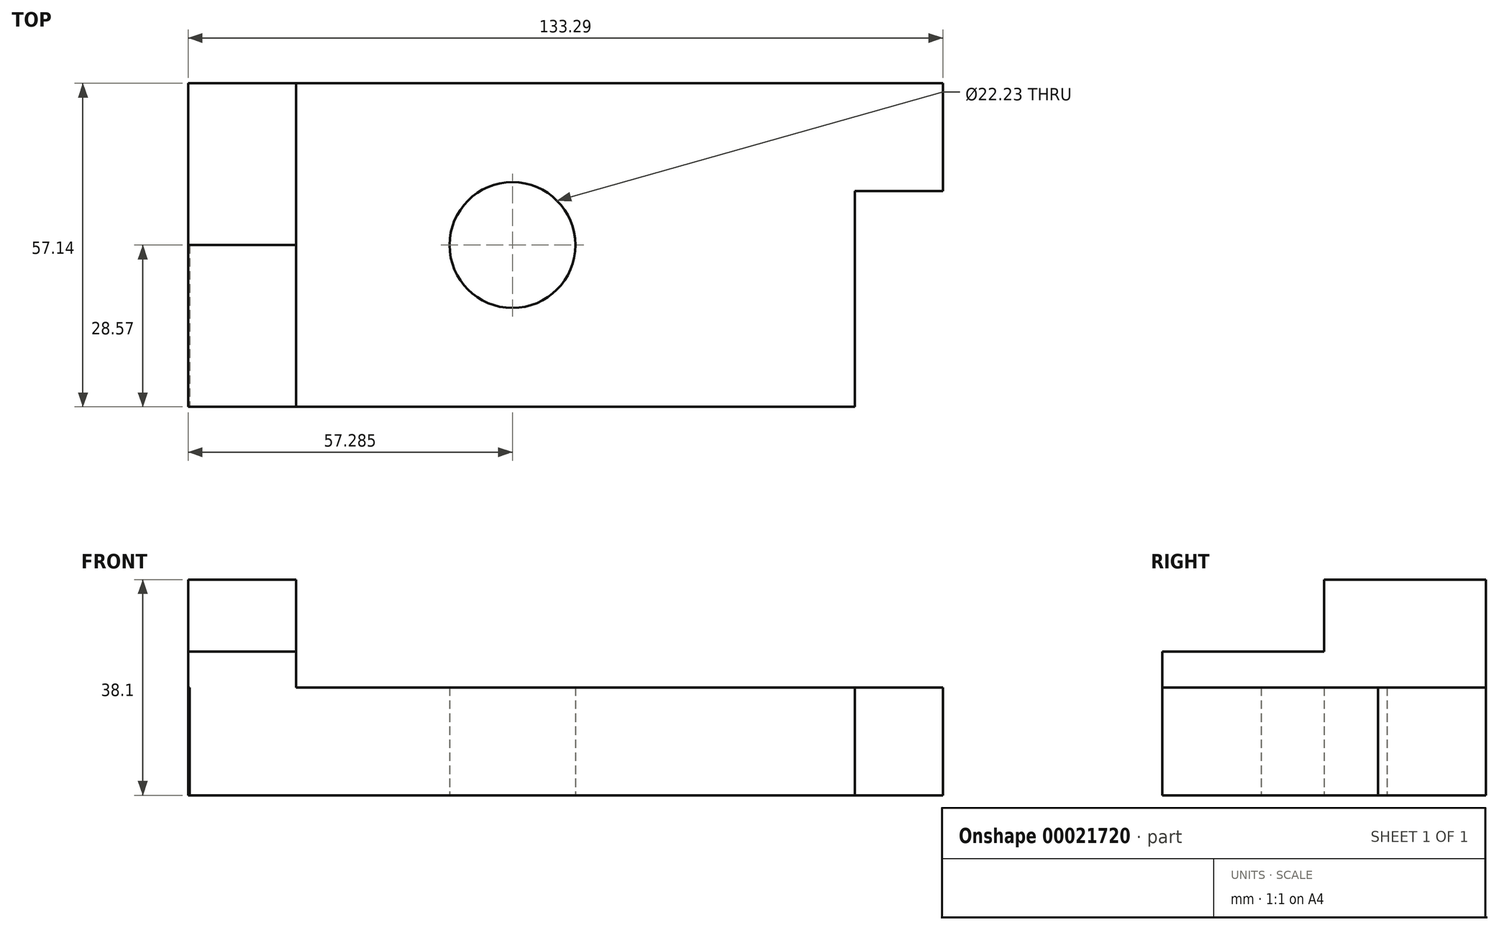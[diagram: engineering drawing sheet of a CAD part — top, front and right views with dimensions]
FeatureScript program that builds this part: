
annotation { "Feature Type Name" : "Feature", "Feature Type Description" : "" }
export const myFeature = defineFeature(function(context is Context, id is Id, definition is map)
    precondition{}
    {
        {
            var Q0;
            Q0=qCreatedBy(makeId("Top.planeOp"),FACE);
            var sketch = newSketch(context, id + "F0", { "sketchPlane" : qUnion([Q0])});
            skLineSegment(sketch, "E0.bottom", {"start": v(0, 0) * mm, "end": v(-0.06, 0) * mm});
            skLineSegment(sketch, "E0.top", {"start": v(0, 28.58) * mm, "end": v(-0.06, 28.58) * mm});
            skLineSegment(sketch, "E0.left", {"start": v(0, 0) * mm, "end": v(0, 28.58) * mm});
            skLineSegment(sketch, "E0.right", {"start": v(-0.06, 0) * mm, "end": v(-0.06, 28.58) * mm});
            skLineSegment(sketch, "E1.bottom", {"start": v(0, 0) * mm, "end": v(114.24, 0) * mm});
            skLineSegment(sketch, "E1.top", {"start": v(0, 28.57) * mm, "end": v(114.24, 28.58) * mm});
            skLineSegment(sketch, "E1.left", {"start": v(0, 0) * mm, "end": v(0, 28.57) * mm});
            skLineSegment(sketch, "E1.right", {"start": v(114.24, 0) * mm, "end": v(114.24, 28.58) * mm});
            skLineSegment(sketch, "E2.bottom", {"start": v(0.27, 0) * mm, "end": v(0, 0) * mm});
            skLineSegment(sketch, "E2.top", {"start": v(0.27, -28.57) * mm, "end": v(0, -28.57) * mm});
            skLineSegment(sketch, "E2.left", {"start": v(0, 0) * mm, "end": v(0, -28.57) * mm});
            skLineSegment(sketch, "E2.right", {"start": v(0.27, 0) * mm, "end": v(0.27, -28.57) * mm});
            skLineSegment(sketch, "E3.bottom", {"start": v(0, 0) * mm, "end": v(114.57, 0) * mm});
            skLineSegment(sketch, "E3.top", {"start": v(0, -28.58) * mm, "end": v(114.57, -28.57) * mm});
            skLineSegment(sketch, "E3.left", {"start": v(0, 0) * mm, "end": v(0, -28.58) * mm});
            skLineSegment(sketch, "E3.right", {"start": v(114.57, 0) * mm, "end": v(114.57, -28.57) * mm});
            skLineSegment(sketch, "E4.bottom", {"start": v(114.57, -28.57) * mm, "end": v(98.7, -28.57) * mm});
            skLineSegment(sketch, "E4.top", {"start": v(114.57, 9.52) * mm, "end": v(98.7, 9.52) * mm});
            skLineSegment(sketch, "E4.left", {"start": v(114.57, -28.57) * mm, "end": v(114.57, 9.52) * mm});
            skLineSegment(sketch, "E4.right", {"start": v(98.7, -28.58) * mm, "end": v(98.7, 9.52) * mm});
            skCircle(sketch, "E5", {"center": v(57.28, 0) * mm, "radius": 11.11 * mm});
            skSolve(sketch);
        }
        {
            var Q0;
            {var subQ12=sQuery(id+"F0.wireOp",EDGE,"E1.top");Q0=makeQuery(id+"F0.imprint","IMPRINT",FACE,{"disambiguationData":[TD([[makeQuery(id+"F0.imprint","IMPRINT",EDGE,{"derivedFrom":subQ12}),-1.0]])]});}
            var Q1;
            {var subQ8=sQuery(id+"F0.wireOp",EDGE,"E2.right");Q1=makeQuery(id+"F0.imprint","IMPRINT",FACE,{"disambiguationData":[TD([[makeQuery(id+"F0.imprint","IMPRINT",EDGE,{"derivedFrom":subQ8}),1.0]])]});}
            extrude(context, id + "F1", {"entities" : qUnion([Q0, Q1]), "depth" : 19.05 * mm});
        }
        {
            var Q0;
            Q0=qCreatedBy(makeId("Right.planeOp"),FACE);
            var sketch = newSketch(context, id + "F2", { "sketchPlane" : qUnion([Q0])});
            skLineSegment(sketch, "E6.bottom", {"start": v(-28.58, 19.05) * mm, "end": v(28.58, 19.05) * mm});
            skLineSegment(sketch, "E6.top", {"start": v(-28.58, 38.1) * mm, "end": v(28.57, 38.1) * mm});
            skLineSegment(sketch, "E6.left", {"start": v(-28.58, 19.05) * mm, "end": v(-28.58, 38.1) * mm});
            skLineSegment(sketch, "E6.right", {"start": v(28.58, 19.05) * mm, "end": v(28.57, 38.1) * mm});
            skLineSegment(sketch, "E7.bottom", {"start": v(-28.58, 38.1) * mm, "end": v(0, 38.1) * mm});
            skLineSegment(sketch, "E7.top", {"start": v(-28.58, 25.4) * mm, "end": v(0, 25.4) * mm});
            skLineSegment(sketch, "E7.left", {"start": v(-28.58, 38.1) * mm, "end": v(-28.58, 25.4) * mm});
            skLineSegment(sketch, "E7.right", {"start": v(0, 38.1) * mm, "end": v(0, 25.4) * mm});
            skSolve(sketch);
        }
        {
            var Q0;
            Q0=makeQuery(id+"F2.imprint","IMPRINT",FACE,{"disambiguationData":[TD([[makeQuery(id+"F2.imprint","IMPRINT",EDGE,{"derivedFrom":sQuery(id+"F2.wireOp",EDGE,"E6.bottom")}),1.0]])]});
            var Q1;
            Q1=makeQuery(id+"F1.opExtrude","SWEPT_FACE",FACE,{"disambiguationData":[OSD([sQuery(id+"F0.wireOp",EDGE,"E1.right")])]});
            var Q2;
            Q2=makeQuery(id+"F1.opExtrude","SWEPT_FACE",FACE,{"disambiguationData":[OSD([sQuery(id+"F0.wireOp",EDGE,"E4.right")])]});
            extrude(context, id + "F3", {"entities" : qUnion([Q0, Q1, Q2]), "operationType" : NewBodyOperationType.ADD, "depth" : 19.05 * mm});
        }
    });
